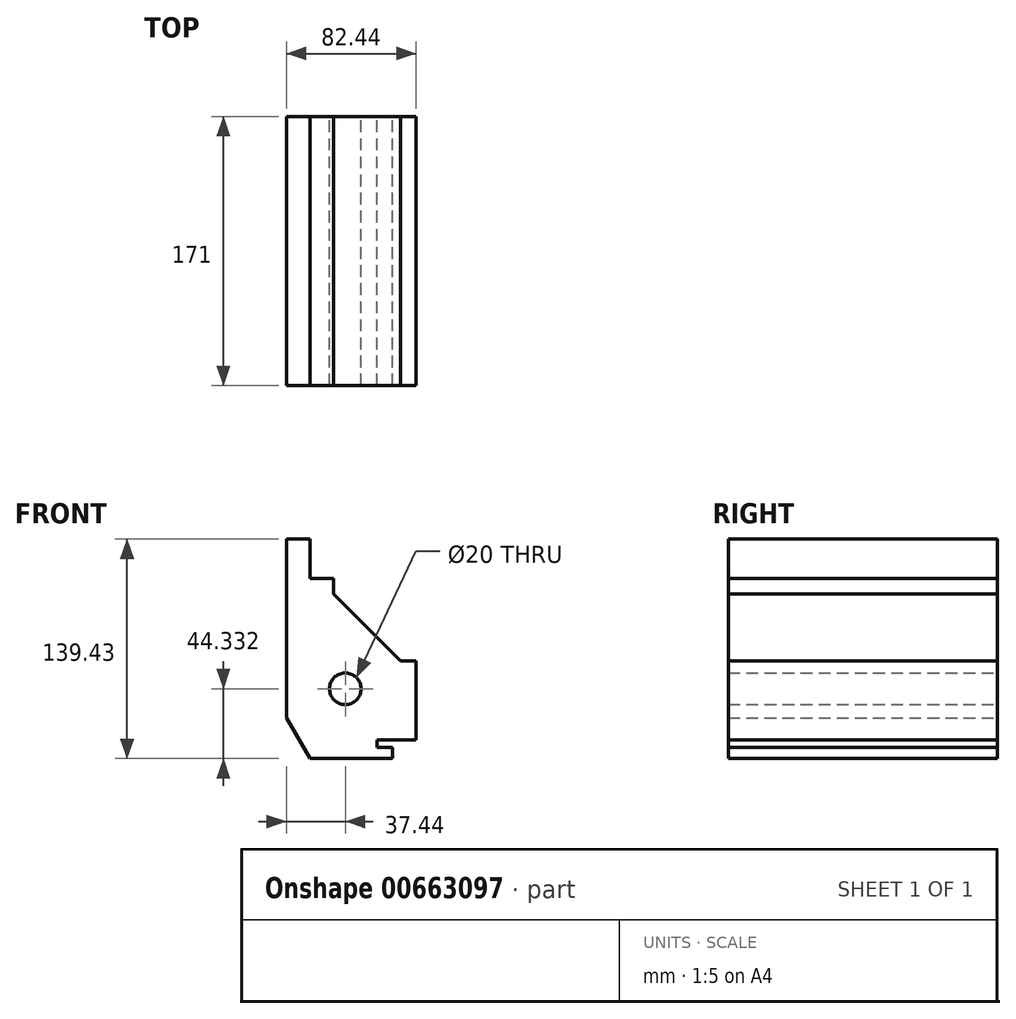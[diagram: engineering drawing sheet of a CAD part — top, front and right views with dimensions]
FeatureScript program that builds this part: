
annotation { "Feature Type Name" : "Feature", "Feature Type Description" : "" }
export const myFeature = defineFeature(function(context is Context, id is Id, definition is map)
    precondition{}
    {
        {
            var Q0;
            Q0=qCreatedBy(makeId("Front.planeOp"),FACE);
            var sketch = newSketch(context, id + "F0", { "sketchPlane" : qUnion([Q0])});
            skLineSegment(sketch, "E0", {"start": v(-15, 139.43) * mm, "end": v(-15, 25.98) * mm});
            skLineSegment(sketch, "E1", {"start": v(-15, 25.98) * mm, "end": v(0, 0) * mm});
            skLineSegment(sketch, "E2", {"start": v(0, 0) * mm, "end": v(52.43, 0) * mm});
            skLineSegment(sketch, "E3", {"start": v(52.43, 0) * mm, "end": v(52.43, 7) * mm});
            skLineSegment(sketch, "E4", {"start": v(52.43, 7) * mm, "end": v(42.43, 7) * mm});
            skLineSegment(sketch, "E5", {"start": v(42.43, 7) * mm, "end": v(42.43, 12) * mm});
            skLineSegment(sketch, "E6", {"start": v(42.43, 12) * mm, "end": v(67.43, 12) * mm});
            skLineSegment(sketch, "E7", {"start": v(67.43, 12) * mm, "end": v(67.43, 62) * mm});
            skLineSegment(sketch, "E8", {"start": v(67.43, 62) * mm, "end": v(57.42, 62) * mm});
            skLineSegment(sketch, "E9", {"start": v(57.42, 62) * mm, "end": v(15, 104.43) * mm});
            skLineSegment(sketch, "E10", {"start": v(15, 104.43) * mm, "end": v(15, 114.43) * mm});
            skLineSegment(sketch, "E11", {"start": v(15, 114.43) * mm, "end": v(0, 114.43) * mm});
            skLineSegment(sketch, "E12", {"start": v(0, 114.43) * mm, "end": v(0, 139.43) * mm});
            skLineSegment(sketch, "E13", {"start": v(0, 139.43) * mm, "end": v(-15, 139.43) * mm});
            skCircle(sketch, "E14", {"center": v(22.43, 44.33) * mm, "radius": 10 * mm});
            skSolve(sketch);
        }
        {
            var Q0;
            Q0=makeQuery(id+"F0.imprint","IMPRINT",FACE,{"disambiguationData":[TD([[makeQuery(id+"F0.imprint","IMPRINT",EDGE,{"derivedFrom":sQuery(id+"F0.wireOp",EDGE,"E0")}),1.0]])]});
            extrude(context, id + "F1", {"entities" : qUnion([Q0]), "depth" : 171 * mm, "offsetDistance" : 25 * mm});
        }
    });
